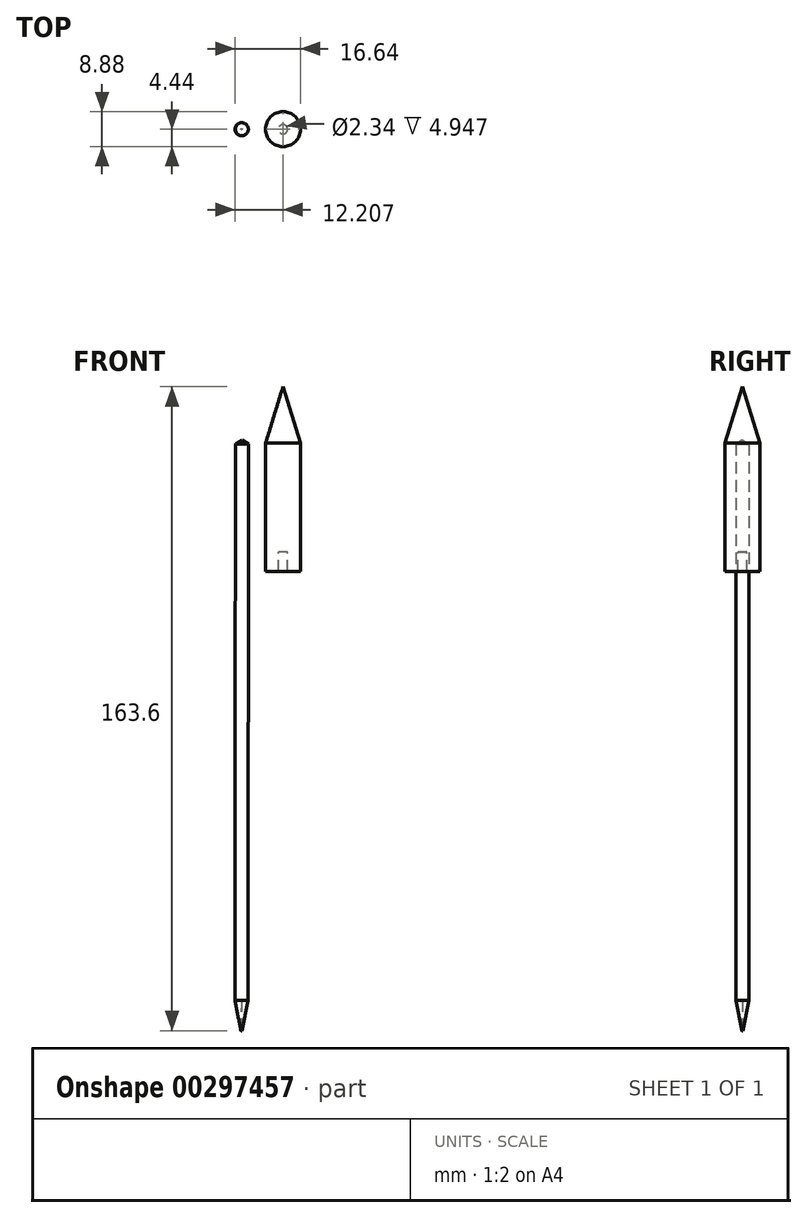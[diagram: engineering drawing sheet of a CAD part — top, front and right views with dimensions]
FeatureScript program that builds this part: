
annotation { "Feature Type Name" : "Feature", "Feature Type Description" : "" }
export const myFeature = defineFeature(function(context is Context, id is Id, definition is map)
    precondition{}
    {
        {
            var Q0;
            Q0=qCreatedBy(makeId("Front.planeOp"),FACE);
            var sketch = newSketch(context, id + "F0", { "sketchPlane" : qUnion([Q0])});
            skLineSegment(sketch, "E0", {"start": v(-39.16, -57.53) * mm, "end": v(-39.05, 83.82) * mm});
            skLineSegment(sketch, "E1", {"start": v(-37.51, -57.53) * mm, "end": v(-37.4, 84.75) * mm});
            skLineSegment(sketch, "E2", {"start": v(-39.16, -57.53) * mm, "end": v(-37.67, -65.29) * mm});
            skLineSegment(sketch, "E3", {"start": v(-37.67, -65.29) * mm, "end": v(-37.51, -57.53) * mm});
            skLineSegment(sketch, "E4", {"start": v(-37.4, 84.75) * mm, "end": v(-39.05, 83.82) * mm});
            skSolve(sketch);
        }
        {
            var Q0;
            Q0 = qSketchRegion(id + "F0", true);
            var Q1;
            Q1=sQuery(id+"F0.wireOp",EDGE,"E1");
            revolve(context, id + "F1", {"entities" : qUnion([Q0]), "axis" : qUnion([Q1]), "revolveType" : RevolveType.FULL});
        }
        {
            var Q0;
            Q0=qCreatedBy(makeId("Front.planeOp"),FACE);
            var sketch = newSketch(context, id + "F2", { "sketchPlane" : qUnion([Q0])});
            skLineSegment(sketch, "E5", {"start": v(-31.39, 84) * mm, "end": v(-31.39, 51.36) * mm});
            skLineSegment(sketch, "E6", {"start": v(-31.39, 84) * mm, "end": v(-26.95, 98.3) * mm});
            skPoint(sketch, "E6.endSnap0", {"position": v(-26.95, 84) * mm});
            skLineSegment(sketch, "E7", {"start": v(-26.95, 98.3) * mm, "end": v(-26.95, 84) * mm});
            skLineSegment(sketch, "E8", {"start": v(-28.12, 51.36) * mm, "end": v(-28.12, 56.3) * mm});
            skLineSegment(sketch, "E9", {"start": v(-28.12, 56.3) * mm, "end": v(-26.95, 56.3) * mm});
            skLineSegment(sketch, "E10", {"start": v(-31.39, 51.36) * mm, "end": v(-28.12, 51.36) * mm});
            skLineSegment(sketch, "E11", {"start": v(-26.95, 84) * mm, "end": v(-26.95, 56.3) * mm});
            skSolve(sketch);
        }
        {
            var Q0;
            Q0 = qSketchRegion(id + "F2", true);
            var Q1;
            Q1=sQuery(id+"F2.wireOp",EDGE,"E11");
            revolve(context, id + "F3", {"entities" : qUnion([Q0]), "axis" : qUnion([Q1]), "revolveType" : RevolveType.FULL});
        }
    });
